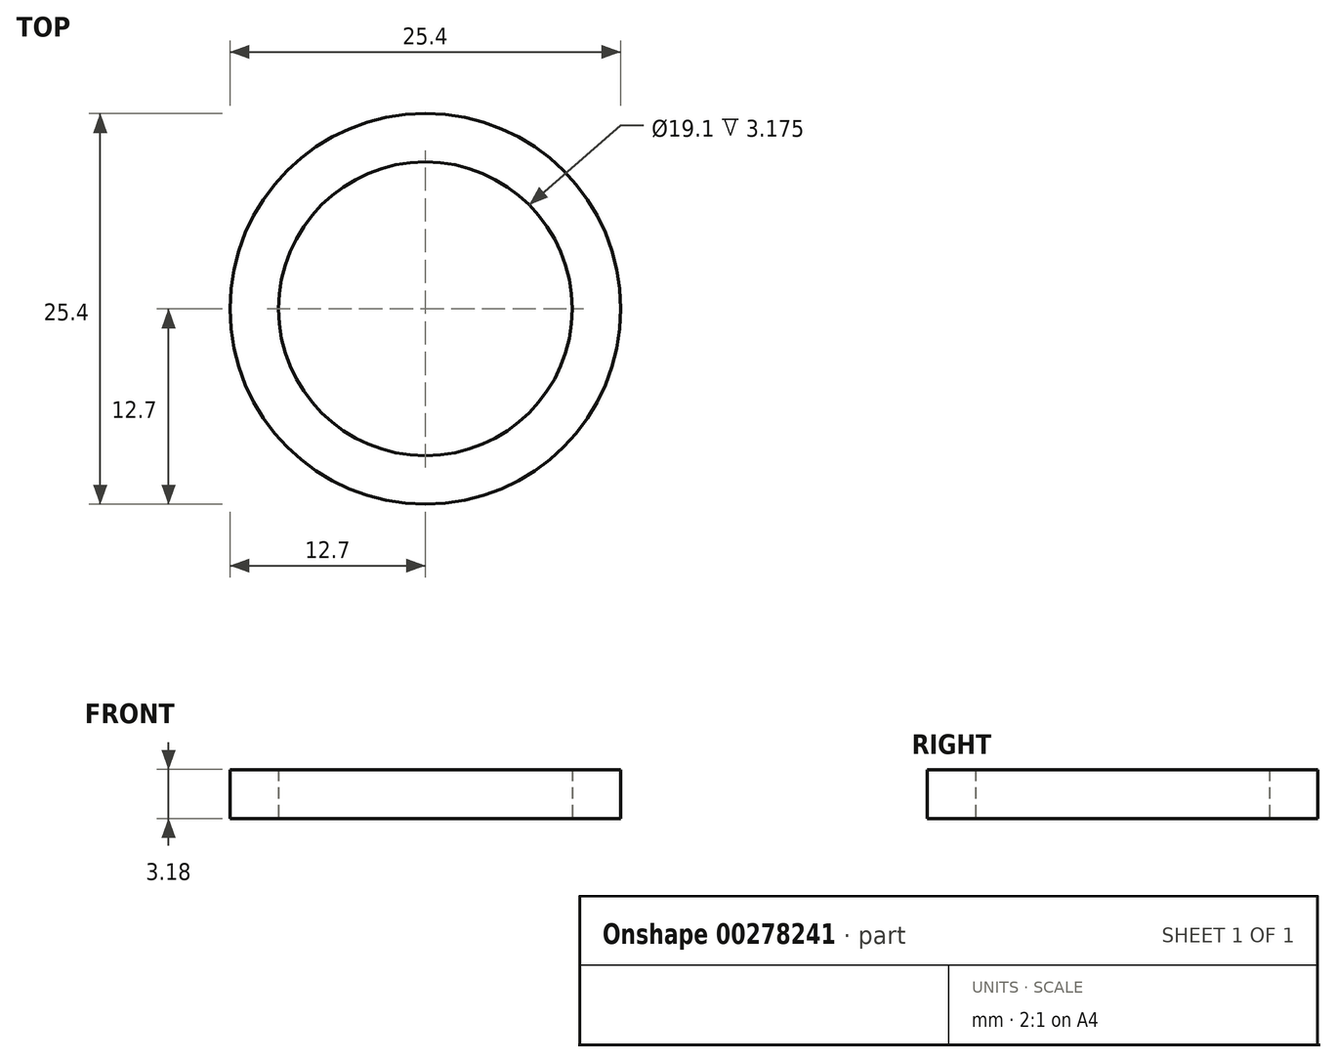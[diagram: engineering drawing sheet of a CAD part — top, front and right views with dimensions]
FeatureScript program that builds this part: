
annotation { "Feature Type Name" : "Feature", "Feature Type Description" : "" }
export const myFeature = defineFeature(function(context is Context, id is Id, definition is map)
    precondition{}
    {
        {
            var Q0;
            Q0=qCreatedBy(makeId("Top.planeOp"),FACE);
            var sketch = newSketch(context, id + "F0", { "sketchPlane" : qUnion([Q0])});
            skCircle(sketch, "E0", {"center": v(0, 0) * mm, "radius": 9.55 * mm});
            skCircle(sketch, "E1", {"center": v(0, 0) * mm, "radius": 12.7 * mm});
            skSolve(sketch);
        }
        {
            var Q0;
            Q0=makeQuery(id+"F0.imprint","IMPRINT",FACE,{"disambiguationData":[TD([[makeQuery(id+"F0.imprint","IMPRINT",EDGE,{"derivedFrom":sQuery(id+"F0.wireOp",EDGE,"E0")}),-1.0]])]});
            extrude(context, id + "F1", {"entities" : qUnion([Q0]), "depth" : 3.17 * mm});
        }
    });
